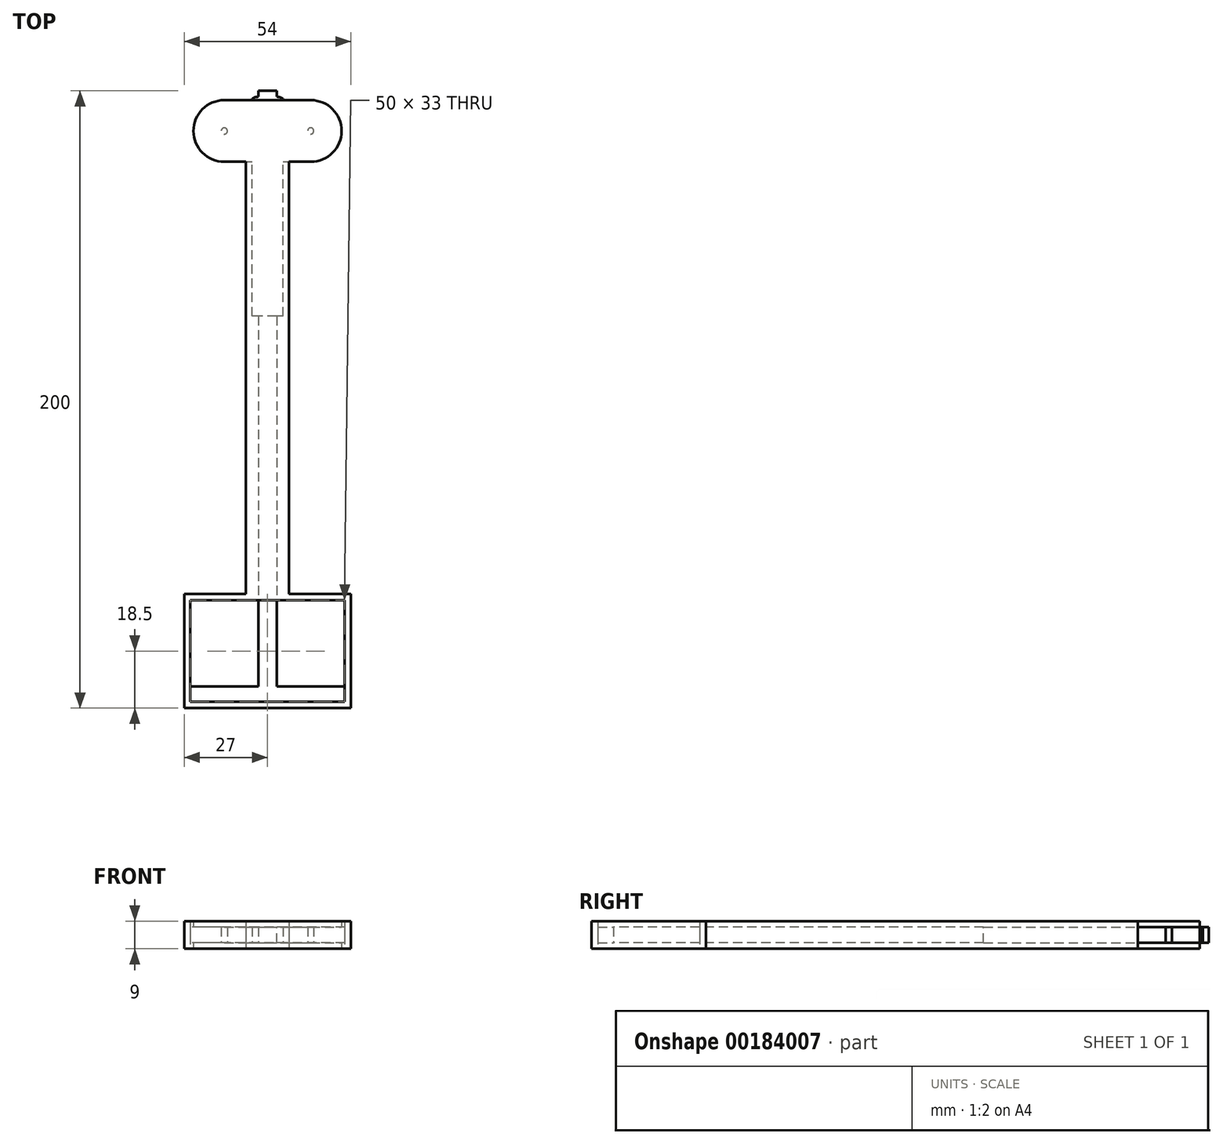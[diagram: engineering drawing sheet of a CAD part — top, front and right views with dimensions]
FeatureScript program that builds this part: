
annotation { "Feature Type Name" : "Feature", "Feature Type Description" : "" }
export const myFeature = defineFeature(function(context is Context, id is Id, definition is map)
    precondition{}
    {
        {
            var Q0;
            Q0=qCreatedBy(makeId("Top.planeOp"),FACE);
            var sketch = newSketch(context, id + "F0", { "sketchPlane" : qUnion([Q0])});
            skLineSegment(sketch, "E0.bottom", {"start": v(0, 13) * mm, "end": v(3, 13) * mm});
            skLineSegment(sketch, "E0.top", {"start": v(0, -180) * mm, "end": v(3, -180) * mm});
            skLineSegment(sketch, "E0.left", {"start": v(0, 13) * mm, "end": v(0, -180) * mm});
            skLineSegment(sketch, "E0.right", {"start": v(3, 13) * mm, "end": v(3, -180) * mm});
            skLineSegment(sketch, "E1", {"start": v(0, 10) * mm, "end": v(3, 10) * mm, "construction": true});
            skArc(sketch, "E2", {"start": v(3, 11.09) * mm, "mid": v(4.04, 10.94) * mm, "end": v(5, 10.5) * mm});
            skLineSegment(sketch, "E3", {"start": v(5, 10.5) * mm, "end": v(5, 10) * mm});
            skArc(sketch, "E4.MirrorCS", {"start": v(3, 8.91) * mm, "mid": v(4.04, 9.06) * mm, "end": v(5, 9.5) * mm});
            skLineSegment(sketch, "E5.MirrorCS", {"start": v(5, 9.5) * mm, "end": v(5, 10) * mm});
            skArc(sketch, "E6.1.0.0", {"start": v(3, 7.89) * mm, "mid": v(4.04, 7.74) * mm, "end": v(5, 7.3) * mm});
            skLineSegment(sketch, "E6.1.0.1", {"start": v(5, 7.3) * mm, "end": v(5, 6.8) * mm});
            skLineSegment(sketch, "E6.1.0.2", {"start": v(5, 6.3) * mm, "end": v(5, 6.8) * mm});
            skArc(sketch, "E6.1.0.3", {"start": v(3, 5.71) * mm, "mid": v(4.04, 5.86) * mm, "end": v(5, 6.3) * mm});
            skArc(sketch, "E6.2.0.0", {"start": v(3, 4.69) * mm, "mid": v(4.04, 4.54) * mm, "end": v(5, 4.1) * mm});
            skLineSegment(sketch, "E6.2.0.1", {"start": v(5, 4.1) * mm, "end": v(5, 3.6) * mm});
            skLineSegment(sketch, "E6.2.0.2", {"start": v(5, 3.1) * mm, "end": v(5, 3.6) * mm});
            skArc(sketch, "E6.2.0.3", {"start": v(3, 2.51) * mm, "mid": v(4.04, 2.66) * mm, "end": v(5, 3.1) * mm});
            skLineSegment(sketch, "E6.direction1", {"start": v(3, 7.39) * mm, "end": v(3, 4.19) * mm, "construction": true});
            skArc(sketch, "E7.0.3.0", {"start": v(3, 1.49) * mm, "mid": v(4.04, 1.34) * mm, "end": v(5, 0.9) * mm});
            skLineSegment(sketch, "E7.4.3.0", {"start": v(5, 0.9) * mm, "end": v(5, 0.4) * mm});
            skLineSegment(sketch, "E7.7.3.0", {"start": v(5, -0.1) * mm, "end": v(5, 0.4) * mm});
            skArc(sketch, "E7.10.3.0", {"start": v(3, -0.69) * mm, "mid": v(4.04, -0.54) * mm, "end": v(5, -0.1) * mm});
            skArc(sketch, "E7.0.4.0", {"start": v(3, -1.71) * mm, "mid": v(4.04, -1.86) * mm, "end": v(5, -2.3) * mm});
            skLineSegment(sketch, "E7.4.4.0", {"start": v(5, -2.3) * mm, "end": v(5, -2.8) * mm});
            skLineSegment(sketch, "E7.7.4.0", {"start": v(5, -3.3) * mm, "end": v(5, -2.8) * mm});
            skArc(sketch, "E7.10.4.0", {"start": v(3, -3.89) * mm, "mid": v(4.04, -3.74) * mm, "end": v(5, -3.3) * mm});
            skArc(sketch, "E7.0.5.0", {"start": v(3, -4.91) * mm, "mid": v(4.04, -5.06) * mm, "end": v(5, -5.5) * mm});
            skLineSegment(sketch, "E7.4.5.0", {"start": v(5, -5.5) * mm, "end": v(5, -6) * mm});
            skLineSegment(sketch, "E7.7.5.0", {"start": v(5, -6.5) * mm, "end": v(5, -6) * mm});
            skArc(sketch, "E7.10.5.0", {"start": v(3, -7.09) * mm, "mid": v(4.04, -6.94) * mm, "end": v(5, -6.5) * mm});
            skArc(sketch, "E7.0.6.0", {"start": v(3, -8.11) * mm, "mid": v(4.04, -8.26) * mm, "end": v(5, -8.7) * mm});
            skLineSegment(sketch, "E7.4.6.0", {"start": v(5, -8.7) * mm, "end": v(5, -9.2) * mm});
            skLineSegment(sketch, "E7.7.6.0", {"start": v(5, -9.7) * mm, "end": v(5, -9.2) * mm});
            skArc(sketch, "E7.10.6.0", {"start": v(3, -10.29) * mm, "mid": v(4.04, -10.14) * mm, "end": v(5, -9.7) * mm});
            skArc(sketch, "E7.0.7.0", {"start": v(3, -11.31) * mm, "mid": v(4.04, -11.46) * mm, "end": v(5, -11.9) * mm});
            skLineSegment(sketch, "E7.4.7.0", {"start": v(5, -11.9) * mm, "end": v(5, -12.4) * mm});
            skLineSegment(sketch, "E7.7.7.0", {"start": v(5, -12.9) * mm, "end": v(5, -12.4) * mm});
            skArc(sketch, "E7.10.7.0", {"start": v(3, -13.49) * mm, "mid": v(4.04, -13.34) * mm, "end": v(5, -12.9) * mm});
            skArc(sketch, "E7.0.8.0", {"start": v(3, -14.51) * mm, "mid": v(4.04, -14.66) * mm, "end": v(5, -15.1) * mm});
            skLineSegment(sketch, "E7.4.8.0", {"start": v(5, -15.1) * mm, "end": v(5, -15.6) * mm});
            skLineSegment(sketch, "E7.7.8.0", {"start": v(5, -16.1) * mm, "end": v(5, -15.6) * mm});
            skArc(sketch, "E7.10.8.0", {"start": v(3, -16.69) * mm, "mid": v(4.04, -16.54) * mm, "end": v(5, -16.1) * mm});
            skArc(sketch, "E7.0.9.0", {"start": v(3, -17.71) * mm, "mid": v(4.04, -17.86) * mm, "end": v(5, -18.3) * mm});
            skLineSegment(sketch, "E7.4.9.0", {"start": v(5, -18.3) * mm, "end": v(5, -18.8) * mm});
            skLineSegment(sketch, "E7.7.9.0", {"start": v(5, -19.3) * mm, "end": v(5, -18.8) * mm});
            skArc(sketch, "E7.10.9.0", {"start": v(3, -19.89) * mm, "mid": v(4.04, -19.74) * mm, "end": v(5, -19.3) * mm});
            skArc(sketch, "E7.0.10.0", {"start": v(3, -20.91) * mm, "mid": v(4.04, -21.06) * mm, "end": v(5, -21.5) * mm});
            skLineSegment(sketch, "E7.4.10.0", {"start": v(5, -21.5) * mm, "end": v(5, -22) * mm});
            skLineSegment(sketch, "E7.7.10.0", {"start": v(5, -22.5) * mm, "end": v(5, -22) * mm});
            skArc(sketch, "E7.10.10.0", {"start": v(3, -23.09) * mm, "mid": v(4.04, -22.94) * mm, "end": v(5, -22.5) * mm});
            skArc(sketch, "E7.0.11.0", {"start": v(3, -24.11) * mm, "mid": v(4.04, -24.26) * mm, "end": v(5, -24.7) * mm});
            skLineSegment(sketch, "E7.4.11.0", {"start": v(5, -24.7) * mm, "end": v(5, -25.2) * mm});
            skLineSegment(sketch, "E7.7.11.0", {"start": v(5, -25.7) * mm, "end": v(5, -25.2) * mm});
            skArc(sketch, "E7.10.11.0", {"start": v(3, -26.29) * mm, "mid": v(4.04, -26.14) * mm, "end": v(5, -25.7) * mm});
            skArc(sketch, "E7.0.12.0", {"start": v(3, -27.31) * mm, "mid": v(4.04, -27.46) * mm, "end": v(5, -27.9) * mm});
            skLineSegment(sketch, "E7.4.12.0", {"start": v(5, -27.9) * mm, "end": v(5, -28.4) * mm});
            skLineSegment(sketch, "E7.7.12.0", {"start": v(5, -28.9) * mm, "end": v(5, -28.4) * mm});
            skArc(sketch, "E7.10.12.0", {"start": v(3, -29.49) * mm, "mid": v(4.04, -29.34) * mm, "end": v(5, -28.9) * mm});
            skArc(sketch, "E7.0.13.0", {"start": v(3, -30.51) * mm, "mid": v(4.04, -30.66) * mm, "end": v(5, -31.1) * mm});
            skLineSegment(sketch, "E7.4.13.0", {"start": v(5, -31.1) * mm, "end": v(5, -31.6) * mm});
            skLineSegment(sketch, "E7.7.13.0", {"start": v(5, -32.1) * mm, "end": v(5, -31.6) * mm});
            skArc(sketch, "E7.10.13.0", {"start": v(3, -32.69) * mm, "mid": v(4.04, -32.54) * mm, "end": v(5, -32.1) * mm});
            skArc(sketch, "E7.0.14.0", {"start": v(3, -33.71) * mm, "mid": v(4.04, -33.86) * mm, "end": v(5, -34.3) * mm});
            skLineSegment(sketch, "E7.4.14.0", {"start": v(5, -34.3) * mm, "end": v(5, -34.8) * mm});
            skLineSegment(sketch, "E7.7.14.0", {"start": v(5, -35.3) * mm, "end": v(5, -34.8) * mm});
            skArc(sketch, "E7.10.14.0", {"start": v(3, -35.89) * mm, "mid": v(4.04, -35.74) * mm, "end": v(5, -35.3) * mm});
            skArc(sketch, "E7.0.15.0", {"start": v(3, -36.91) * mm, "mid": v(4.04, -37.06) * mm, "end": v(5, -37.5) * mm});
            skLineSegment(sketch, "E7.4.15.0", {"start": v(5, -37.5) * mm, "end": v(5, -38) * mm});
            skLineSegment(sketch, "E7.7.15.0", {"start": v(5, -38.5) * mm, "end": v(5, -38) * mm});
            skArc(sketch, "E7.10.15.0", {"start": v(3, -39.09) * mm, "mid": v(4.04, -38.94) * mm, "end": v(5, -38.5) * mm});
            skSolve(sketch);
        }
        {
            var Q0;
            Q0 = qSketchRegion(id + "F0", true);
            extrude(context, id + "F1", {"entities" : qUnion([Q0]), "depth" : 5 * mm});
        }
        {
            var Q0;
            Q0=makeQuery(id+"F1.opExtrude","SWEPT_BODY",BODY,{"disambiguationData":[OSD([sQuery(id+"F0.wireOp",EDGE,"E0.bottom"),sQuery(id+"F0.wireOp",EDGE,"E0.top"),sQuery(id+"F0.wireOp",EDGE,"E0.left"),sQuery(id+"F0.wireOp",EDGE,"E0.right"),sQuery(id+"F0.wireOp",EDGE,"E2"),sQuery(id+"F0.wireOp",EDGE,"E3"),sQuery(id+"F0.wireOp",EDGE,"E4.MirrorCS"),sQuery(id+"F0.wireOp",EDGE,"E5.MirrorCS"),sQuery(id+"F0.wireOp",EDGE,"E6.1.0.0"),sQuery(id+"F0.wireOp",EDGE,"E6.1.0.1"),sQuery(id+"F0.wireOp",EDGE,"E6.1.0.2"),sQuery(id+"F0.wireOp",EDGE,"E6.1.0.3"),sQuery(id+"F0.wireOp",EDGE,"E6.2.0.0"),sQuery(id+"F0.wireOp",EDGE,"E6.2.0.1"),sQuery(id+"F0.wireOp",EDGE,"E6.2.0.2"),sQuery(id+"F0.wireOp",EDGE,"E6.2.0.3"),sQuery(id+"F0.wireOp",EDGE,"E7.0.3.0"),sQuery(id+"F0.wireOp",EDGE,"E7.4.3.0"),sQuery(id+"F0.wireOp",EDGE,"E7.7.3.0"),sQuery(id+"F0.wireOp",EDGE,"E7.10.3.0"),sQuery(id+"F0.wireOp",EDGE,"E7.0.4.0"),sQuery(id+"F0.wireOp",EDGE,"E7.4.4.0"),sQuery(id+"F0.wireOp",EDGE,"E7.7.4.0"),sQuery(id+"F0.wireOp",EDGE,"E7.10.4.0"),sQuery(id+"F0.wireOp",EDGE,"E7.0.5.0"),sQuery(id+"F0.wireOp",EDGE,"E7.4.5.0"),sQuery(id+"F0.wireOp",EDGE,"E7.7.5.0"),sQuery(id+"F0.wireOp",EDGE,"E7.10.5.0"),sQuery(id+"F0.wireOp",EDGE,"E7.0.6.0"),sQuery(id+"F0.wireOp",EDGE,"E7.4.6.0"),sQuery(id+"F0.wireOp",EDGE,"E7.7.6.0"),sQuery(id+"F0.wireOp",EDGE,"E7.10.6.0"),sQuery(id+"F0.wireOp",EDGE,"E7.0.7.0"),sQuery(id+"F0.wireOp",EDGE,"E7.4.7.0"),sQuery(id+"F0.wireOp",EDGE,"E7.7.7.0"),sQuery(id+"F0.wireOp",EDGE,"E7.10.7.0"),sQuery(id+"F0.wireOp",EDGE,"E7.0.8.0"),sQuery(id+"F0.wireOp",EDGE,"E7.4.8.0"),sQuery(id+"F0.wireOp",EDGE,"E7.7.8.0"),sQuery(id+"F0.wireOp",EDGE,"E7.10.8.0"),sQuery(id+"F0.wireOp",EDGE,"E7.0.9.0"),sQuery(id+"F0.wireOp",EDGE,"E7.4.9.0"),sQuery(id+"F0.wireOp",EDGE,"E7.7.9.0"),sQuery(id+"F0.wireOp",EDGE,"E7.10.9.0"),sQuery(id+"F0.wireOp",EDGE,"E7.0.10.0"),sQuery(id+"F0.wireOp",EDGE,"E7.4.10.0"),sQuery(id+"F0.wireOp",EDGE,"E7.7.10.0"),sQuery(id+"F0.wireOp",EDGE,"E7.10.10.0"),sQuery(id+"F0.wireOp",EDGE,"E7.0.11.0"),sQuery(id+"F0.wireOp",EDGE,"E7.4.11.0"),sQuery(id+"F0.wireOp",EDGE,"E7.7.11.0"),sQuery(id+"F0.wireOp",EDGE,"E7.10.11.0"),sQuery(id+"F0.wireOp",EDGE,"E7.0.12.0"),sQuery(id+"F0.wireOp",EDGE,"E7.4.12.0"),sQuery(id+"F0.wireOp",EDGE,"E7.7.12.0"),sQuery(id+"F0.wireOp",EDGE,"E7.10.12.0"),sQuery(id+"F0.wireOp",EDGE,"E7.0.13.0"),sQuery(id+"F0.wireOp",EDGE,"E7.4.13.0"),sQuery(id+"F0.wireOp",EDGE,"E7.7.13.0"),sQuery(id+"F0.wireOp",EDGE,"E7.10.13.0"),sQuery(id+"F0.wireOp",EDGE,"E7.0.14.0"),sQuery(id+"F0.wireOp",EDGE,"E7.4.14.0"),sQuery(id+"F0.wireOp",EDGE,"E7.7.14.0"),sQuery(id+"F0.wireOp",EDGE,"E7.10.14.0"),sQuery(id+"F0.wireOp",EDGE,"E7.0.15.0"),sQuery(id+"F0.wireOp",EDGE,"E7.4.15.0"),sQuery(id+"F0.wireOp",EDGE,"E7.7.15.0"),sQuery(id+"F0.wireOp",EDGE,"E7.10.15.0")])]});
            var Q1;
            Q1=makeQuery(id+"F1.opExtrude","SWEPT_FACE",FACE,{"disambiguationData":[OSD([sQuery(id+"F0.wireOp",EDGE,"E0.left")])]});
            mirror(context, id + "F2", {"operationType" : NewBodyOperationType.ADD, "entities" : qUnion([Q0]), "mirrorPlane" : qUnion([Q1])});
        }
        {
            var Q0;
            {var subQ0=makeQuery(id+"F1.opExtrude","SWEPT_FACE",FACE,{"disambiguationData":[OSD([sQuery(id+"F0.wireOp",EDGE,"E0.top")])]});Q0=makeQuery(id+"F2.boolean.opBoolean","MERGE",FACE,{"derivedFrom":[subQ0,makeQuery(id+"F2.opPattern","COPY",FACE,{"derivedFrom":subQ0,"instanceName":"1"})]});}
            var sketch = newSketch(context, id + "F3", { "sketchPlane" : qUnion([Q0])});
            skLineSegment(sketch, "E8.bottom", {"start": v(25, 5) * mm, "end": v(-25, 5) * mm});
            skLineSegment(sketch, "E8.top", {"start": v(25, 0) * mm, "end": v(-25, 0) * mm});
            skLineSegment(sketch, "E8.left", {"start": v(25, 5) * mm, "end": v(25, 0) * mm});
            skLineSegment(sketch, "E8.right", {"start": v(-25, 5) * mm, "end": v(-25, 0) * mm});
            skPoint(sketch, "E8.middle", {"position": v(0, 2.5) * mm});
            skPoint(sketch, "E8.middle.positionSnap0", {"position": v(-3, 2.5) * mm});
            skPoint(sketch, "E8.middle.positionSnap1", {"position": v(0, 0) * mm});
            skPoint(sketch, "E8.centerSnap0", {"position": v(-3, 2.5) * mm});
            skPoint(sketch, "E8.centerSnap1", {"position": v(0, 0) * mm});
            skSolve(sketch);
        }
        {
            var Q0;
            Q0 = qSketchRegion(id + "F3", true);
            extrude(context, id + "F4", {"entities" : qUnion([Q0]), "operationType" : NewBodyOperationType.ADD, "depth" : 5 * mm});
        }
        {
            var Q0;
            Q0=qCreatedBy(makeId("Top.planeOp"),FACE);
            var sketch = newSketch(context, id + "F5", { "sketchPlane" : qUnion([Q0])});
            skCircle(sketch, "E9", {"center": v(14, 0) * mm, "radius": 10 * mm});
            skLineSegment(sketch, "E10", {"start": v(0, 10) * mm, "end": v(14, 10) * mm});
            skLineSegment(sketch, "E11", {"start": v(14, -10) * mm, "end": v(7, -10) * mm});
            skLineSegment(sketch, "E12", {"start": v(7, -10) * mm, "end": v(7, -150) * mm});
            skLineSegment(sketch, "E13", {"start": v(7, -150) * mm, "end": v(27, -150) * mm});
            skLineSegment(sketch, "E14", {"start": v(27, -150) * mm, "end": v(27, -187) * mm});
            skLineSegment(sketch, "E15", {"start": v(27, -187) * mm, "end": v(0, -187) * mm});
            skCircle(sketch, "E16.MirrorC", {"center": v(-14, 0) * mm, "radius": 10 * mm});
            skLineSegment(sketch, "E17.MirrorCS", {"start": v(0, 10) * mm, "end": v(-14, 10) * mm});
            skLineSegment(sketch, "E18.MirrorCS", {"start": v(-14, -10) * mm, "end": v(-7, -10) * mm});
            skLineSegment(sketch, "E19.MirrorCS", {"start": v(-7, -10) * mm, "end": v(-7, -150) * mm});
            skLineSegment(sketch, "E20.MirrorCS", {"start": v(-7, -150) * mm, "end": v(-27, -150) * mm});
            skLineSegment(sketch, "E21.MirrorCS", {"start": v(-27, -150) * mm, "end": v(-27, -187) * mm});
            skLineSegment(sketch, "E22.MirrorCS", {"start": v(-27, -187) * mm, "end": v(0, -187) * mm});
            skLineSegment(sketch, "E23.bottom", {"start": v(-25, -152) * mm, "end": v(25, -152) * mm});
            skLineSegment(sketch, "E23.top", {"start": v(-25, -185) * mm, "end": v(25, -185) * mm});
            skLineSegment(sketch, "E23.left", {"start": v(-25, -152) * mm, "end": v(-25, -185) * mm});
            skLineSegment(sketch, "E23.right", {"start": v(25, -152) * mm, "end": v(25, -185) * mm});
            skPoint(sketch, "E23.middle", {"position": v(0, -168.5) * mm});
            skSolve(sketch);
        }
        {
            var Q0;
            Q0 = qSketchRegion(id + "F5", true);
            extrude(context, id + "F6", {"entities" : qUnion([Q0]), "depth" : 7 * mm, "hasSecondDirection" : true, "secondDirectionOppositeDirection" : true, "secondDirectionDepth" : 2 * mm});
        }
        {
            var Q0;
            Q0=makeQuery(id+"F1.opExtrude","SWEPT_BODY",BODY,{"disambiguationData":[OSD([sQuery(id+"F0.wireOp",EDGE,"E0.bottom"),sQuery(id+"F0.wireOp",EDGE,"E0.top"),sQuery(id+"F0.wireOp",EDGE,"E0.left"),sQuery(id+"F0.wireOp",EDGE,"E0.right"),sQuery(id+"F0.wireOp",EDGE,"E2"),sQuery(id+"F0.wireOp",EDGE,"E3"),sQuery(id+"F0.wireOp",EDGE,"E4.MirrorCS"),sQuery(id+"F0.wireOp",EDGE,"E5.MirrorCS"),sQuery(id+"F0.wireOp",EDGE,"E6.1.0.0"),sQuery(id+"F0.wireOp",EDGE,"E6.1.0.1"),sQuery(id+"F0.wireOp",EDGE,"E6.1.0.2"),sQuery(id+"F0.wireOp",EDGE,"E6.1.0.3"),sQuery(id+"F0.wireOp",EDGE,"E6.2.0.0"),sQuery(id+"F0.wireOp",EDGE,"E6.2.0.1"),sQuery(id+"F0.wireOp",EDGE,"E6.2.0.2"),sQuery(id+"F0.wireOp",EDGE,"E6.2.0.3"),sQuery(id+"F0.wireOp",EDGE,"E7.0.3.0"),sQuery(id+"F0.wireOp",EDGE,"E7.4.3.0"),sQuery(id+"F0.wireOp",EDGE,"E7.7.3.0"),sQuery(id+"F0.wireOp",EDGE,"E7.10.3.0"),sQuery(id+"F0.wireOp",EDGE,"E7.0.4.0"),sQuery(id+"F0.wireOp",EDGE,"E7.4.4.0"),sQuery(id+"F0.wireOp",EDGE,"E7.7.4.0"),sQuery(id+"F0.wireOp",EDGE,"E7.10.4.0"),sQuery(id+"F0.wireOp",EDGE,"E7.0.5.0"),sQuery(id+"F0.wireOp",EDGE,"E7.4.5.0"),sQuery(id+"F0.wireOp",EDGE,"E7.7.5.0"),sQuery(id+"F0.wireOp",EDGE,"E7.10.5.0"),sQuery(id+"F0.wireOp",EDGE,"E7.0.6.0"),sQuery(id+"F0.wireOp",EDGE,"E7.4.6.0"),sQuery(id+"F0.wireOp",EDGE,"E7.7.6.0"),sQuery(id+"F0.wireOp",EDGE,"E7.10.6.0"),sQuery(id+"F0.wireOp",EDGE,"E7.0.7.0"),sQuery(id+"F0.wireOp",EDGE,"E7.4.7.0"),sQuery(id+"F0.wireOp",EDGE,"E7.7.7.0"),sQuery(id+"F0.wireOp",EDGE,"E7.10.7.0"),sQuery(id+"F0.wireOp",EDGE,"E7.0.8.0"),sQuery(id+"F0.wireOp",EDGE,"E7.4.8.0"),sQuery(id+"F0.wireOp",EDGE,"E7.7.8.0"),sQuery(id+"F0.wireOp",EDGE,"E7.10.8.0"),sQuery(id+"F0.wireOp",EDGE,"E7.0.9.0"),sQuery(id+"F0.wireOp",EDGE,"E7.4.9.0"),sQuery(id+"F0.wireOp",EDGE,"E7.7.9.0"),sQuery(id+"F0.wireOp",EDGE,"E7.10.9.0"),sQuery(id+"F0.wireOp",EDGE,"E7.0.10.0"),sQuery(id+"F0.wireOp",EDGE,"E7.4.10.0"),sQuery(id+"F0.wireOp",EDGE,"E7.7.10.0"),sQuery(id+"F0.wireOp",EDGE,"E7.10.10.0"),sQuery(id+"F0.wireOp",EDGE,"E7.0.11.0"),sQuery(id+"F0.wireOp",EDGE,"E7.4.11.0"),sQuery(id+"F0.wireOp",EDGE,"E7.7.11.0"),sQuery(id+"F0.wireOp",EDGE,"E7.10.11.0"),sQuery(id+"F0.wireOp",EDGE,"E7.0.12.0"),sQuery(id+"F0.wireOp",EDGE,"E7.4.12.0"),sQuery(id+"F0.wireOp",EDGE,"E7.7.12.0"),sQuery(id+"F0.wireOp",EDGE,"E7.10.12.0"),sQuery(id+"F0.wireOp",EDGE,"E7.0.13.0"),sQuery(id+"F0.wireOp",EDGE,"E7.4.13.0"),sQuery(id+"F0.wireOp",EDGE,"E7.7.13.0"),sQuery(id+"F0.wireOp",EDGE,"E7.10.13.0"),sQuery(id+"F0.wireOp",EDGE,"E7.0.14.0"),sQuery(id+"F0.wireOp",EDGE,"E7.4.14.0"),sQuery(id+"F0.wireOp",EDGE,"E7.7.14.0"),sQuery(id+"F0.wireOp",EDGE,"E7.10.14.0"),sQuery(id+"F0.wireOp",EDGE,"E7.0.15.0"),sQuery(id+"F0.wireOp",EDGE,"E7.4.15.0"),sQuery(id+"F0.wireOp",EDGE,"E7.7.15.0"),sQuery(id+"F0.wireOp",EDGE,"E7.10.15.0")])]});
            var Q1;
            Q1=makeQuery(id+"F6.opExtrude","SWEPT_BODY",BODY,{"disambiguationData":[OSD([sQuery(id+"F5.wireOp",EDGE,"E9"),sQuery(id+"F5.wireOp",EDGE,"E10"),sQuery(id+"F5.wireOp",EDGE,"E11"),sQuery(id+"F5.wireOp",EDGE,"E12"),sQuery(id+"F5.wireOp",EDGE,"E13"),sQuery(id+"F5.wireOp",EDGE,"E14"),sQuery(id+"F5.wireOp",EDGE,"E15"),sQuery(id+"F5.wireOp",EDGE,"E16.MirrorC"),sQuery(id+"F5.wireOp",EDGE,"E17.MirrorCS"),sQuery(id+"F5.wireOp",EDGE,"E18.MirrorCS"),sQuery(id+"F5.wireOp",EDGE,"E19.MirrorCS"),sQuery(id+"F5.wireOp",EDGE,"E20.MirrorCS"),sQuery(id+"F5.wireOp",EDGE,"E21.MirrorCS"),sQuery(id+"F5.wireOp",EDGE,"E22.MirrorCS"),sQuery(id+"F5.wireOp",EDGE,"E23.bottom"),sQuery(id+"F5.wireOp",EDGE,"E23.top"),sQuery(id+"F5.wireOp",EDGE,"E23.left"),sQuery(id+"F5.wireOp",EDGE,"E23.right")])]});
            booleanBodies(context, id + "F7", {"operationType" : BooleanOperationType.SUBTRACTION, "tools" : qUnion([Q0]), "targets" : qUnion([Q1]), "keepTools" : true});
        }
        {
            var Q0;
            Q0=qCreatedBy(makeId("Top.planeOp"),FACE);
            var sketch = newSketch(context, id + "F8", { "sketchPlane" : qUnion([Q0])});
            skArc(sketch, "E24.0", {"start": v(-14, -10) * mm, "mid": v(-24, 0) * mm, "end": v(-14, 10) * mm});
            skLineSegment(sketch, "E25.0", {"start": v(-14, 10) * mm, "end": v(14, 10) * mm});
            skArc(sketch, "E26.0", {"start": v(14, -10) * mm, "mid": v(24, 0) * mm, "end": v(14, 10) * mm});
            skLineSegment(sketch, "E27", {"start": v(-14, -10) * mm, "end": v(14, -10) * mm});
            skSolve(sketch);
        }
        {
            var Q0;
            Q0 = qSketchRegion(id + "F8", true);
            extrude(context, id + "F9", {"entities" : qUnion([Q0]), "operationType" : NewBodyOperationType.REMOVE, "depth" : 5 * mm});
        }
        {
            var Q0;
            {var subQ69=sQuery(id+"F8.wireOp",EDGE,"E27");Q0=makeQuery(id+"F9.boolean.opBoolean","COPY",FACE,{"disambiguationData":[TD([makeQuery(id+"F6.opExtrude","SWEPT_FACE",FACE,{"disambiguationData":[OSD([sQuery(id+"F5.wireOp",EDGE,"E18.MirrorCS")])]})])],"derivedFrom":makeQuery(id+"F9.opExtrude","SWEPT_FACE",FACE,{"disambiguationData":[OSD([subQ69])]})});}
            var sketch = newSketch(context, id + "F10", { "sketchPlane" : qUnion([Q0])});
            skLineSegment(sketch, "E28.bottom", {"start": v(-5, 5) * mm, "end": v(5, 5) * mm});
            skLineSegment(sketch, "E28.top", {"start": v(-5, 0) * mm, "end": v(5, 0) * mm});
            skLineSegment(sketch, "E28.left", {"start": v(-5, 5) * mm, "end": v(-5, 0) * mm});
            skLineSegment(sketch, "E28.right", {"start": v(5, 5) * mm, "end": v(5, 0) * mm});
            skSolve(sketch);
        }
        {
            var Q0;
            Q0 = qSketchRegion(id + "F10", true);
            extrude(context, id + "F11", {"entities" : qUnion([Q0]), "operationType" : NewBodyOperationType.REMOVE, "oppositeDirection" : true, "depth" : 50 * mm});
        }
        {
            var Q0;
            Q0=qCreatedBy(makeId("Top.planeOp"),FACE);
            var sketch = newSketch(context, id + "F12", { "sketchPlane" : qUnion([Q0])});
            skCircle(sketch, "E29", {"center": v(-14, 0) * mm, "radius": 1 * mm});
            skCircle(sketch, "E30", {"center": v(14, 0) * mm, "radius": 1 * mm});
            skSolve(sketch);
        }
        {
            var Q0;
            Q0 = qSketchRegion(id + "F12", true);
            extrude(context, id + "F13", {"entities" : qUnion([Q0]), "operationType" : NewBodyOperationType.ADD, "endBound" : BoundingType.UP_TO_NEXT, "depth" : 25 * mm});
        }
    });
